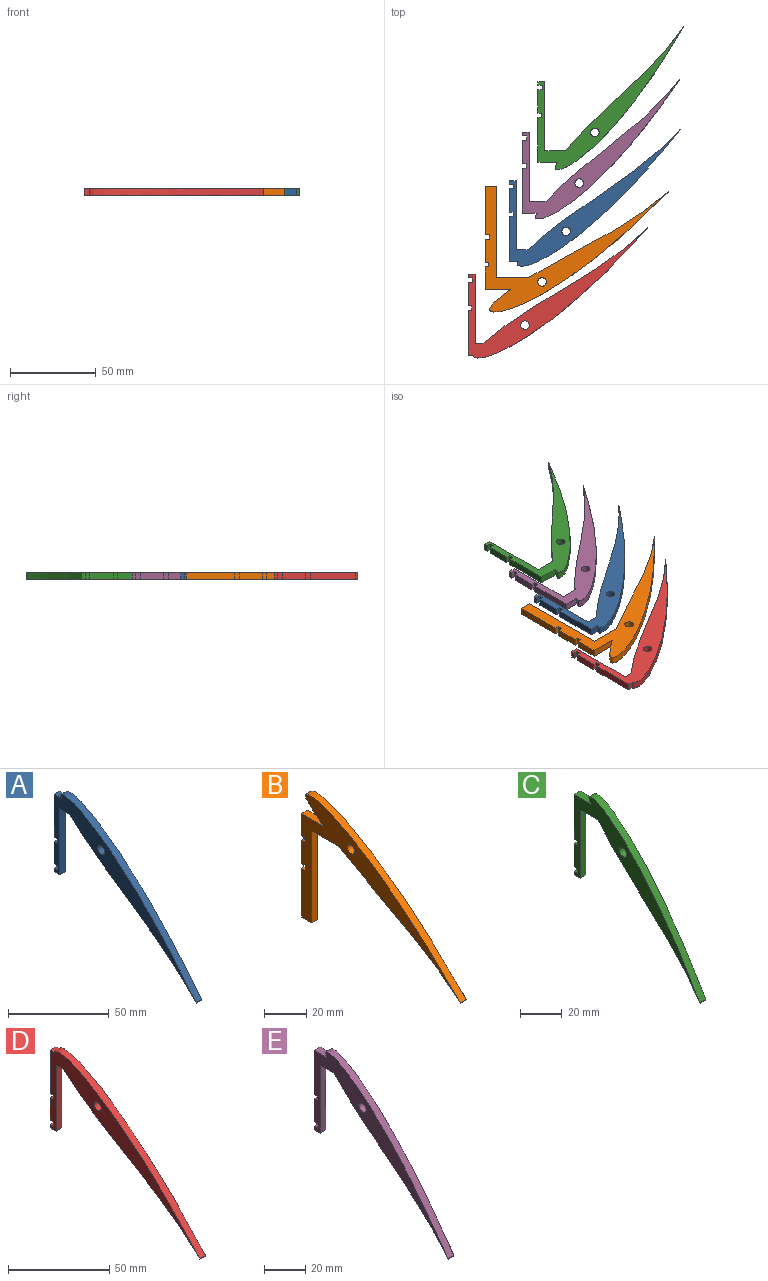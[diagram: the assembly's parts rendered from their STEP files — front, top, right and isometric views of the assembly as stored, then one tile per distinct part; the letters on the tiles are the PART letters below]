
ASSEMBLY  parts=5 mates=4
PART A: 17 faces, bbox 4x99.6x79.8 mm
  f0: plane 13.63x4mm, normal (0,1,0), area 54.5mm2, adj f2,f3,f11,f15
  f1: plane 4x2.01mm, normal (0,1,0), area 8mm2, adj f2,f3,f8,f10
  f2: plane 99.64x79.8mm, normal (-1,0,0), area 1300.1mm2, adj f0,f1,f4,f5,f6,f7,f8,f9
  f3: plane 99.64x79.8mm, normal (1,0,0), area 1300.1mm2, adj f0,f1,f4,f5,f6,f7,f8,f9
  f4: extruded ~94.35x79.4mm, area 971.2mm2, adj f2,f3,f5,f6
  f5: plane 6.91x4mm, normal (0,0,-1), area 27.7mm2, adj f2,f3,f4,f9
  f6: plane 5.24x4mm, normal (0,0,1), area 21mm2, adj f2,f3,f4,f7
  f7: plane 26.11x4mm, normal (0,1,0), area 104.4mm2, adj f2,f3,f6,f13
  f8: plane 4.03x4mm, normal (0,0,-1), area 16.1mm2, adj f1,f2,f3,f9
  f9: plane 40.17x4mm, normal (0,-1,0), area 160.7mm2, adj f2,f3,f5,f8
  f10: plane 4x2.41mm, normal (0,0,1), area 9.6mm2, adj f1,f2,f3,f12
  f11: plane 4x2.41mm, normal (0,0,-1), area 9.6mm2, adj f0,f2,f3,f12
  f12: plane 4x2.64mm, normal (0,1,0), area 10.5mm2, adj f2,f3,f10,f11
  f13: plane 4x2.18mm, normal (0,0,-1), area 8.7mm2, adj f2,f3,f7,f14
  f14: plane 4x2.52mm, normal (0,1,0), area 10.1mm2, adj f2,f3,f13,f15
  f15: plane 4x2.18mm, normal (0,0,1), area 8.7mm2, adj f0,f2,f3,f14
  f16: cylinder r=2.5mm len=5mm, axis (1,0,0), area 62.8mm2, adj f2,f3
PART B: 17 faces, bbox 4x106.5x73.3 mm
  f0: plane 13.63x4mm, normal (0,1,0), area 54.5mm2, adj f2,f3,f11,f15
  f1: plane 28.27x4mm, normal (0,1,0), area 113.1mm2, adj f2,f3,f9,f10
  f2: plane 106.55x73.28mm, normal (-1,0,0), area 1908.1mm2, adj f0,f1,f4,f5,f6,f7,f8,f9
  f3: plane 106.55x73.28mm, normal (1,0,0), area 1908.1mm2, adj f0,f1,f4,f5,f6,f7,f8,f9
  f4: extruded ~101.53x68.39mm, area 965.7mm2, adj f2,f3,f5,f7
  f5: plane 14.98x4mm, normal (0,0,1), area 59.9mm2, adj f2,f3,f4,f8
  f6: plane 53.49x4mm, normal (0,-1,0), area 214mm2, adj f2,f3,f7,f9
  f7: plane 18.12x4mm, normal (0,0,-1), area 72.5mm2, adj f2,f3,f4,f6
  f8: plane 12.99x4mm, normal (0,1,0), area 51.9mm2, adj f2,f3,f5,f13
  f9: plane 6.75x4mm, normal (0,0,-1), area 27mm2, adj f1,f2,f3,f6
  f10: plane 4x2.41mm, normal (0,0,1), area 9.6mm2, adj f1,f2,f3,f12
  f11: plane 4x2.41mm, normal (0,0,-1), area 9.6mm2, adj f0,f2,f3,f12
  f12: plane 4x2.64mm, normal (0,1,0), area 10.5mm2, adj f2,f3,f10,f11
  f13: plane 4x2.18mm, normal (0,0,-1), area 8.7mm2, adj f2,f3,f8,f14
  f14: plane 4x2.52mm, normal (0,1,0), area 10.1mm2, adj f2,f3,f13,f15
  f15: plane 4x2.18mm, normal (0,0,1), area 8.7mm2, adj f0,f2,f3,f14
  f16: cylinder r=2.5mm len=5mm, axis (1,0,0), area 62.8mm2, adj f2,f3
PART C: 17 faces, bbox 4x84.9x83.4 mm
  f0: plane 13.63x4mm, normal (0,1,0), area 54.5mm2, adj f2,f3,f11,f15
  f1: plane 4x2.01mm, normal (0,1,0), area 8mm2, adj f2,f3,f9,f10
  f2: plane 84.88x83.4mm, normal (-1,0,0), area 848.5mm2, adj f0,f1,f4,f5,f6,f7,f8,f9
  f3: plane 84.88x83.4mm, normal (1,0,0), area 848.5mm2, adj f0,f1,f4,f5,f6,f7,f8,f9
  f4: extruded ~81.38x72.41mm, area 881.2mm2, adj f2,f3,f5,f7
  f5: plane 12x4mm, normal (0,0,-1), area 48mm2, adj f2,f3,f4,f6
  f6: plane 40.17x4mm, normal (0,-1,0), area 160.7mm2, adj f2,f3,f5,f9
  f7: plane 11.32x4mm, normal (0,0,1), area 45.3mm2, adj f2,f3,f4,f8
  f8: plane 26.11x4mm, normal (0,1,0), area 104.4mm2, adj f2,f3,f7,f13
  f9: plane 4.03x4mm, normal (0,0,-1), area 16.1mm2, adj f1,f2,f3,f6
  f10: plane 4x2.41mm, normal (0,0,1), area 9.6mm2, adj f1,f2,f3,f12
  f11: plane 4x2.41mm, normal (0,0,-1), area 9.6mm2, adj f0,f2,f3,f12
  f12: plane 4x2.64mm, normal (0,1,0), area 10.5mm2, adj f2,f3,f10,f11
  f13: plane 4x2.18mm, normal (0,0,-1), area 8.7mm2, adj f2,f3,f8,f14
  f14: plane 4x2.52mm, normal (0,1,0), area 10.1mm2, adj f2,f3,f13,f15
  f15: plane 4x2.18mm, normal (0,0,1), area 8.7mm2, adj f0,f2,f3,f14
  f16: cylinder r=2.5mm len=5mm, axis (1,0,0), area 62.8mm2, adj f2,f3
PART D: 17 faces, bbox 4x104.6x75.8 mm
  f0: plane 13.63x4mm, normal (0,1,0), area 54.5mm2, adj f2,f3,f11,f15
  f1: plane 4x2.01mm, normal (0,1,0), area 8mm2, adj f2,f3,f8,f10
  f2: plane 104.58x75.78mm, normal (-1,0,0), area 1004.9mm2, adj f0,f1,f4,f5,f6,f7,f8,f9
  f3: plane 104.58x75.78mm, normal (1,0,0), area 1004.9mm2, adj f0,f1,f4,f5,f6,f7,f8,f9
  f4: extruded ~100.64x74.24mm, area 990.5mm2, adj f2,f3,f5,f6
  f5: plane 4.6x4mm, normal (0,0,-1), area 18.4mm2, adj f2,f3,f4,f9
  f6: plane 4x2.91mm, normal (0,0,1), area 11.6mm2, adj f2,f3,f4,f7
  f7: plane 26.11x4mm, normal (0,1,0), area 104.4mm2, adj f2,f3,f6,f13
  f8: plane 4.03x4mm, normal (0,0,-1), area 16.1mm2, adj f1,f2,f3,f9
  f9: plane 40.17x4mm, normal (0,-1,0), area 160.7mm2, adj f2,f3,f5,f8
  f10: plane 4x2.41mm, normal (0,0,1), area 9.6mm2, adj f1,f2,f3,f12
  f11: plane 4x2.41mm, normal (0,0,-1), area 9.6mm2, adj f0,f2,f3,f12
  f12: plane 4x2.64mm, normal (0,1,0), area 10.5mm2, adj f2,f3,f10,f11
  f13: plane 4x2.18mm, normal (0,0,-1), area 8.7mm2, adj f2,f3,f7,f14
  f14: plane 4x2.52mm, normal (0,1,0), area 10.1mm2, adj f2,f3,f13,f15
  f15: plane 4x2.18mm, normal (0,0,1), area 8.7mm2, adj f0,f2,f3,f14
  f16: cylinder r=2.5mm len=5mm, axis (1,0,0), area 62.8mm2, adj f2,f3
PART E: 17 faces, bbox 4x91.5x81 mm
  f0: plane 13.63x4mm, normal (0,1,0), area 54.5mm2, adj f2,f3,f11,f15
  f1: plane 4x2.01mm, normal (0,1,0), area 8mm2, adj f2,f3,f8,f10
  f2: plane 91.53x81.04mm, normal (-1,0,0), area 1097.1mm2, adj f0,f1,f4,f5,f6,f7,f8,f9
  f3: plane 91.53x81.04mm, normal (1,0,0), area 1097.1mm2, adj f0,f1,f4,f5,f6,f7,f8,f9
  f4: extruded ~82.3x79.81mm, area 912.2mm2, adj f2,f3,f5,f6
  f5: plane 9.73x4mm, normal (0,0,-1), area 38.9mm2, adj f2,f3,f4,f9
  f6: plane 8.56x4mm, normal (0,0,1), area 34.2mm2, adj f2,f3,f4,f7
  f7: plane 26.11x4mm, normal (0,1,0), area 104.4mm2, adj f2,f3,f6,f13
  f8: plane 4.03x4mm, normal (0,0,-1), area 16.1mm2, adj f1,f2,f3,f9
  f9: plane 40.17x4mm, normal (0,-1,0), area 160.7mm2, adj f2,f3,f5,f8
  f10: plane 4x2.41mm, normal (0,0,1), area 9.6mm2, adj f1,f2,f3,f12
  f11: plane 4x2.41mm, normal (0,0,-1), area 9.6mm2, adj f0,f2,f3,f12
  f12: plane 4x2.64mm, normal (0,1,0), area 10.5mm2, adj f2,f3,f10,f11
  f13: plane 4x2.18mm, normal (0,0,-1), area 8.7mm2, adj f2,f3,f7,f14
  f14: plane 4x2.52mm, normal (0,1,0), area 10.1mm2, adj f2,f3,f13,f15
  f15: plane 4x2.18mm, normal (0,0,1), area 8.7mm2, adj f0,f2,f3,f14
  f16: cylinder r=2.5mm len=5mm, axis (1,0,0), area 62.8mm2, adj f2,f3
PLACE A rot(axis=(0.58,-0.58,0.58),120deg) t=(59.49,-50.28,1093.14)mm
PLACE B rot(axis=(0.58,-0.58,0.58),120deg) t=(45.47,-79.66,1297.14)mm
PLACE C rot(axis=(0.58,-0.58,0.58),120deg) t=(76.18,7.31,889.14)mm
PLACE D rot(axis=(0.58,-0.58,0.58),120deg) t=(35.57,-104.83,1195.14)mm
PLACE E rot(axis=(0.58,-0.58,0.58),120deg) t=(67.11,-22.22,991.14)mm
MATE planar D.f3 <-> A.f3  axis (0,0,1) through (39.38,-97.54,181.14)mm
MATE planar A.f3 <-> E.f3  axis (0,0,1) through (62.01,-42.98,181.14)mm
MATE planar E.f3 <-> C.f3  axis (0,0,1) through (67.39,-15.33,181.14)mm
MATE planar B.f3 <-> D.f3  axis (0,0,1) through (43.11,-67.62,181.14)mm
